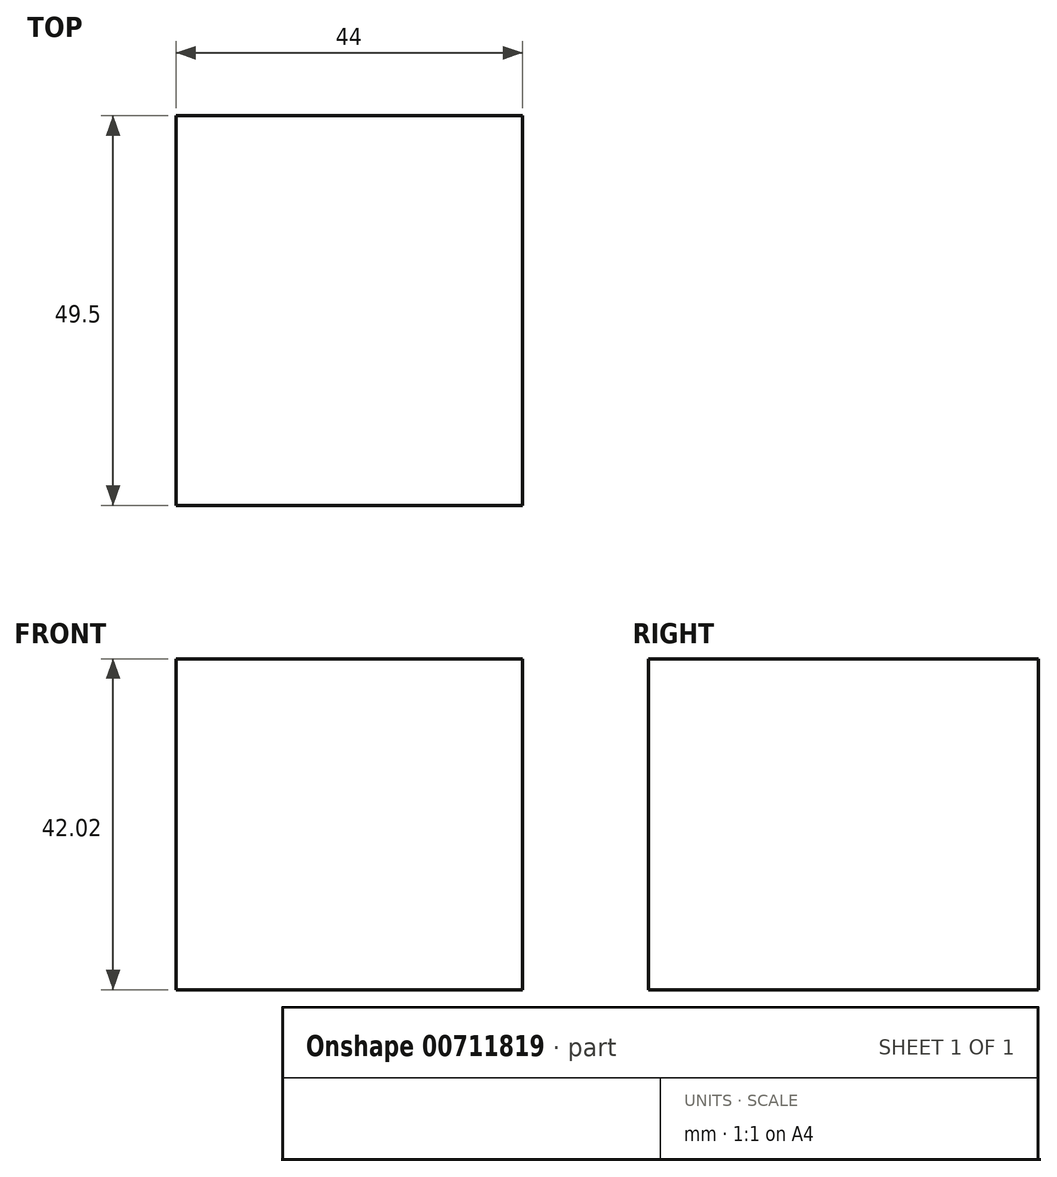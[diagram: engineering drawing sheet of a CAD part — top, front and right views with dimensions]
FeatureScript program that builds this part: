
annotation { "Feature Type Name" : "Feature", "Feature Type Description" : "" }
export const myFeature = defineFeature(function(context is Context, id is Id, definition is map)
    precondition{}
    {
        {
            var Q0;
            Q0=qCreatedBy(makeId("Front.planeOp"),FACE);
            var sketch = newSketch(context, id + "F0", { "sketchPlane" : qUnion([Q0])});
            skLineSegment(sketch, "E0.bottom", {"start": v(-22, 21) * mm, "end": v(22, 21) * mm});
            skLineSegment(sketch, "E0.top", {"start": v(-22, -21) * mm, "end": v(22, -21) * mm});
            skLineSegment(sketch, "E0.left", {"start": v(-22, 21) * mm, "end": v(-22, -21) * mm});
            skLineSegment(sketch, "E0.right", {"start": v(22, 21) * mm, "end": v(22, -21) * mm});
            skPoint(sketch, "E0.middle", {"position": v(0, 0) * mm});
            skSolve(sketch);
        }
        {
            var Q0;
            Q0=qCreatedBy(makeId("Front.planeOp"),FACE);
            var sketch = newSketch(context, id + "F1", { "sketchPlane" : qUnion([Q0])});
            skSolve(sketch);
        }
        {
            var Q0;
            Q0 = qSketchRegion(id + "F1", true);
            var Q1;
            Q1=makeQuery(id+"F0.imprint","IMPRINT",FACE,{"disambiguationData":[TD([[makeQuery(id+"F0.imprint","IMPRINT",EDGE,{"derivedFrom":sQuery(id+"F0.wireOp",EDGE,"E0.bottom")}),-1.0]])]});
            extrude(context, id + "F2", {"entities" : qUnion([Q0, Q1]), "depth" : 0 * mm, "offsetDistance" : 25.4 * mm, "hasSecondDirection" : true, "secondDirectionOppositeDirection" : true, "secondDirectionDepth" : 49.5 * mm});
        }
    });
